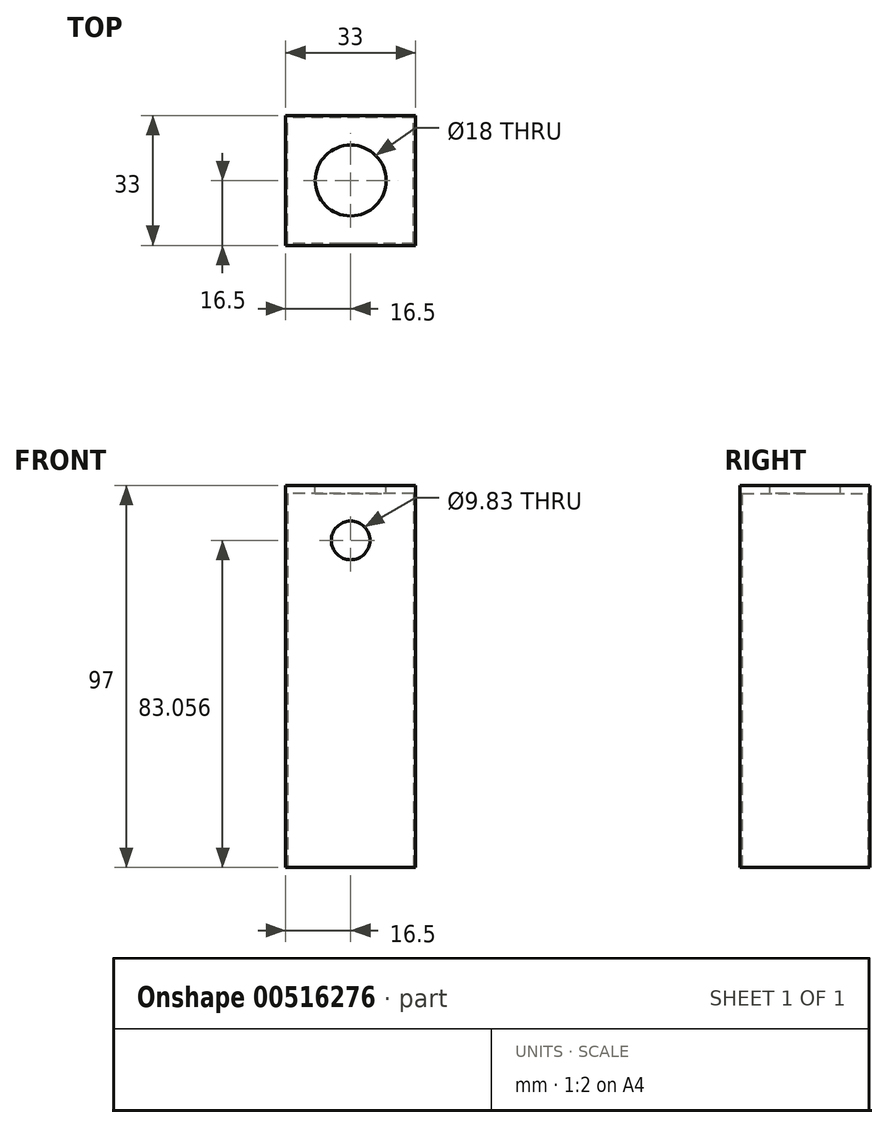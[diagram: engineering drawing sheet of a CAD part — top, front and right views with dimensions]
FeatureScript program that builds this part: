
annotation { "Feature Type Name" : "Feature", "Feature Type Description" : "" }
export const myFeature = defineFeature(function(context is Context, id is Id, definition is map)
    precondition{}
    {
        {
            var Q0;
            Q0=qCreatedBy(makeId("Top.planeOp"),FACE);
            var sketch = newSketch(context, id + "F0", { "sketchPlane" : qUnion([Q0])});
            skLineSegment(sketch, "E0.bottom", {"start": v(16.5, 16.5) * mm, "end": v(-16.5, 16.5) * mm});
            skLineSegment(sketch, "E0.top", {"start": v(16.5, -16.5) * mm, "end": v(-16.5, -16.5) * mm});
            skLineSegment(sketch, "E0.left", {"start": v(16.5, 16.5) * mm, "end": v(16.5, -16.5) * mm});
            skLineSegment(sketch, "E0.right", {"start": v(-16.5, 16.5) * mm, "end": v(-16.5, -16.5) * mm});
            skPoint(sketch, "E0.middle", {"position": v(0, 0) * mm});
            skSolve(sketch);
        }
        {
            var Q0;
            Q0 = qSketchRegion(id + "F0", true);
            var Q1;
            Q1=makeQuery(id+"F0.imprint","IMPRINT",FACE,{"disambiguationData":[TD([[makeQuery(id+"F0.imprint","IMPRINT",EDGE,{"derivedFrom":sQuery(id+"F0.wireOp",EDGE,"E0.bottom")}),1.0]])]});
            extrude(context, id + "F1", {"entities" : qUnion([Q0, Q1]), "depth" : 96 * mm, "offsetDistance" : 25 * mm});
        }
        {
            var Q0;
            Q0=makeQuery(id+"F1.opExtrude","CAP_FACE",FACE,{"disambiguationData":[OSD([sQuery(id+"F0.wireOp",EDGE,"E0.bottom"),sQuery(id+"F0.wireOp",EDGE,"E0.top"),sQuery(id+"F0.wireOp",EDGE,"E0.left"),sQuery(id+"F0.wireOp",EDGE,"E0.right")])],"isStart":true});
            var sketch = newSketch(context, id + "F2", { "sketchPlane" : qUnion([Q0])});
            skLineSegment(sketch, "E1.bottom", {"start": v(16, 16) * mm, "end": v(-16, 16) * mm});
            skLineSegment(sketch, "E1.top", {"start": v(16, -16) * mm, "end": v(-16, -16) * mm});
            skLineSegment(sketch, "E1.left", {"start": v(16, 16) * mm, "end": v(16, -16) * mm});
            skLineSegment(sketch, "E1.right", {"start": v(-16, 16) * mm, "end": v(-16, -16) * mm});
            skPoint(sketch, "E1.middle", {"position": v(0, 0) * mm});
            skSolve(sketch);
        }
        {
            var Q0;
            Q0=makeQuery(id+"F2.imprint","IMPRINT",FACE,{"disambiguationData":[TD([[makeQuery(id+"F2.imprint","IMPRINT",EDGE,{"derivedFrom":sQuery(id+"F2.wireOp",EDGE,"E1.bottom")}),1.0]])]});
            extrude(context, id + "F3", {"entities" : qUnion([Q0]), "operationType" : NewBodyOperationType.REMOVE, "oppositeDirection" : true, "depth" : 95 * mm, "offsetDistance" : 25 * mm});
        }
        {
            var Q0;
            Q0=makeQuery(id+"F1.opExtrude","CAP_FACE",FACE,{"disambiguationData":[OSD([sQuery(id+"F0.wireOp",EDGE,"E0.bottom"),sQuery(id+"F0.wireOp",EDGE,"E0.top"),sQuery(id+"F0.wireOp",EDGE,"E0.left"),sQuery(id+"F0.wireOp",EDGE,"E0.right")])],"isStart":false});
            var sketch = newSketch(context, id + "F4", { "sketchPlane" : qUnion([Q0])});
            skCircle(sketch, "E2", {"center": v(0, 0) * mm, "radius": 9 * mm});
            skSolve(sketch);
        }
        {
            var Q0;
            Q0 = qSketchRegion(id + "F4", true);
            extrude(context, id + "F5", {"entities" : qUnion([Q0]), "operationType" : NewBodyOperationType.REMOVE, "oppositeDirection" : true, "depth" : 2 * mm, "offsetDistance" : 25 * mm});
        }
        {
            var Q0;
            {var subQ0=sQuery(id+"F0.wireOp",EDGE,"E0.right");var subQ1=sQuery(id+"F0.wireOp",EDGE,"E0.bottom");var subQ2=sQuery(id+"F0.wireOp",EDGE,"E0.left");Q0=makeQuery(id+"FcE59dP1X9MsoSQ_1.boolean.opBoolean","MERGE",FACE,{"derivedFrom":[makeQuery(id+"FjEZ2uSFmfVRaE5_1.boolean.opBoolean","MERGE",FACE,{"derivedFrom":[makeQuery(id+"FnSyRhq95FrRzFl_1.boolean.opBoolean","MERGE",FACE,{"derivedFrom":[makeQuery(id+"F1.opExtrude","CAP_FACE",FACE,{"disambiguationData":[OSD([subQ1,sQuery(id+"F0.wireOp",EDGE,"E0.top"),subQ2,subQ0])],"isStart":false}),makeQuery(id+"FnSyRhq95FrRzFl_1.opExtrude","SWEPT_FACE",FACE,{"disambiguationData":[OSD([subQ2]),TDD([makeQuery(id+"F1.opExtrude","CAP_EDGE",EDGE,{"disambiguationData":[OSD([subQ2])],"isStart":false})])]})]}),makeQuery(id+"FjEZ2uSFmfVRaE5_1.opExtrude","SWEPT_FACE",FACE,{"disambiguationData":[OSD([subQ1,subQ2]),TDD([makeQuery(id+"FnSyRhq95FrRzFl_1.boolean.opBoolean","MERGE",EDGE,{"derivedFrom":[makeQuery(id+"F1.opExtrude","CAP_EDGE",EDGE,{"disambiguationData":[OSD([subQ1])],"isStart":false}),makeQuery(id+"FnSyRhq95FrRzFl_1.opExtrude","SWEPT_EDGE",EDGE,{"disambiguationData":[OSD([subQ1,subQ2]),TDD([makeQuery(id+"F1.opExtrude","CAP_VERTEX",VERTEX,{"disambiguationData":[OSD([subQ1,subQ2])],"isStart":false})])]})]})])]})]}),makeQuery(id+"FcE59dP1X9MsoSQ_1.opExtrude","SWEPT_FACE",FACE,{"disambiguationData":[OSD([subQ1,subQ0]),TDD([makeQuery(id+"FjEZ2uSFmfVRaE5_1.boolean.opBoolean","MERGE",EDGE,{"derivedFrom":[makeQuery(id+"F1.opExtrude","CAP_EDGE",EDGE,{"disambiguationData":[OSD([subQ0])],"isStart":false}),makeQuery(id+"FjEZ2uSFmfVRaE5_1.opExtrude","SWEPT_EDGE",EDGE,{"disambiguationData":[OSD([subQ1,subQ0]),TDD([makeQuery(id+"F1.opExtrude","CAP_VERTEX",VERTEX,{"disambiguationData":[OSD([subQ1,subQ0])],"isStart":false})])]})]})])]})]});}
            extrude(context, id + "F6", {"entities" : qUnion([Q0]), "operationType" : NewBodyOperationType.ADD, "depth" : 1 * mm, "offsetDistance" : 25 * mm});
        }
        {
            var Q0;
            {var subQ0=sQuery(id+"F0.wireOp",EDGE,"E0.top");Q0=makeQuery(id+"F6.boolean.opBoolean","MERGE",FACE,{"derivedFrom":[makeQuery(id+"F1.opExtrude","SWEPT_FACE",FACE,{"disambiguationData":[OSD([subQ0])]}),makeQuery(id+"F6.opExtrude","SWEPT_FACE",FACE,{"disambiguationData":[OSD([subQ0])]})]});}
            var sketch = newSketch(context, id + "F7", { "sketchPlane" : qUnion([Q0])});
            skCircle(sketch, "E3", {"center": v(0, 83.06) * mm, "radius": 4.91 * mm});
            skSolve(sketch);
        }
        {
            var Q0;
            Q0=makeQuery(id+"F7.imprint","IMPRINT",FACE,{"disambiguationData":[TD([[makeQuery(id+"F7.imprint","IMPRINT",EDGE,{"derivedFrom":sQuery(id+"F7.wireOp",EDGE,"E3")}),1.0]])]});
            extrude(context, id + "F8", {"entities" : qUnion([Q0]), "operationType" : NewBodyOperationType.REMOVE, "oppositeDirection" : true, "depth" : 25 * mm, "offsetDistance" : 25 * mm});
        }
    });
